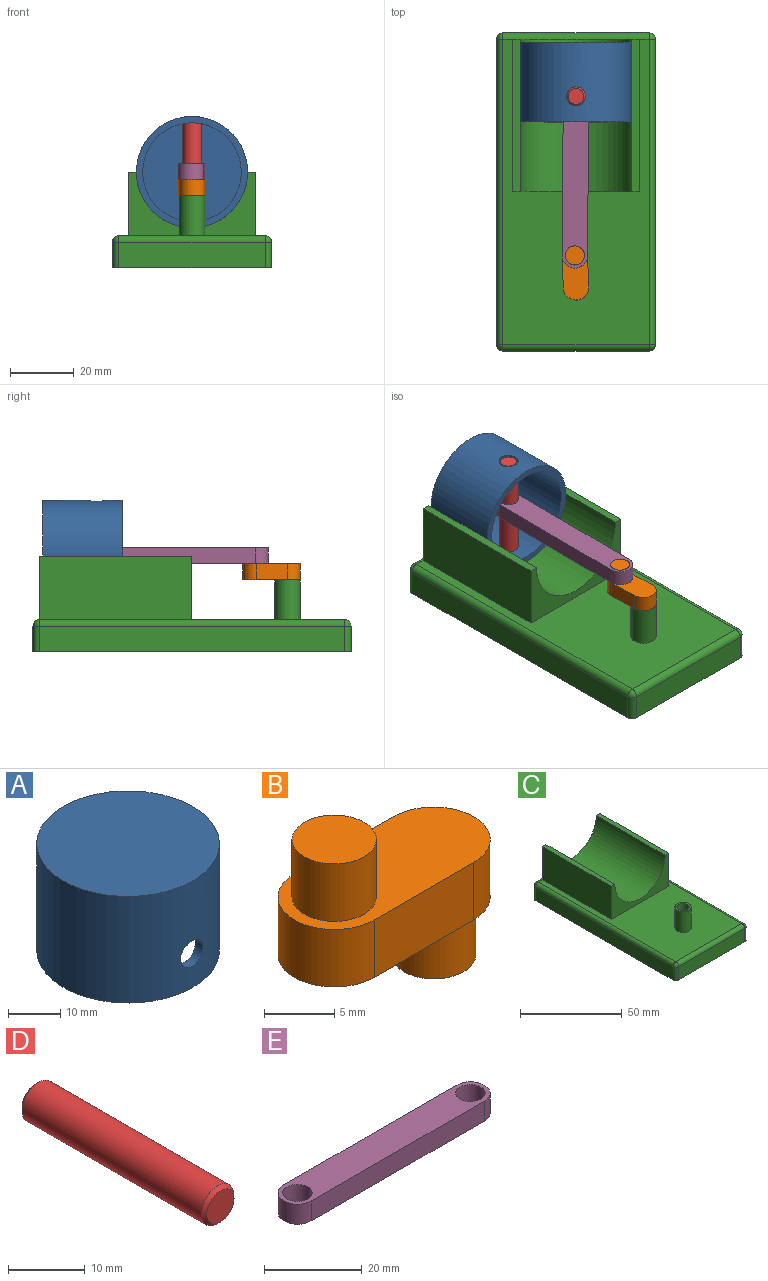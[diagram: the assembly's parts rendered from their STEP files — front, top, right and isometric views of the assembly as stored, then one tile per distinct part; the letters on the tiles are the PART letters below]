
ASSEMBLY  parts=5 mates=5
PART A: 7 faces, bbox 35x35x25 mm
  f0: cylinder r=17.5mm len=35mm, axis (0,0,-1), area 2691.8mm2, adj f1,f2,f5,f6
  f1: plane 35x35mm, normal (0,0,1), area 962.1mm2, adj f0
  f2: plane 35x35mm, normal (0,0,-1), area 207.3mm2, adj f0,f3
  f3: cylinder r=15.5mm len=31mm, axis (0,0,-1), area 2182.9mm2, adj f2,f4,f5,f6
  f4: plane 31x31mm, normal (0,0,-1), area 754.8mm2, adj f3
  f5: cylinder r=3mm len=6mm, axis (0,-1,0), area 38mm2, adj f0,f3
  f6: cylinder r=3mm len=6mm, axis (0,-1,0), area 38mm2, adj f0,f3
PART B: 10 faces, bbox 18x8x15 mm
  f0: cylinder r=4mm len=8mm, axis (0,0,-1), area 62.8mm2, adj f1,f3,f4,f5
  f1: plane 10x5mm, normal (0,1,0), area 50mm2, adj f0,f2,f4,f5
  f2: cylinder r=4mm len=8mm, axis (0,0,-1), area 62.8mm2, adj f1,f3,f4,f5
  f3: plane 10x5mm, normal (0,-1,0), area 50mm2, adj f0,f2,f4,f5
  f4: plane 18x8mm, normal (0,0,1), area 102mm2, adj f0,f1,f2,f3,f6
  f5: plane 18x8mm, normal (0,0,-1), area 102mm2, adj f0,f1,f2,f3,f8
  f6: cylinder r=3mm len=6mm, axis (0,0,-1), area 94.2mm2, adj f4,f7
  f7: plane 6x6mm, normal (0,0,1), area 28.3mm2, adj f6
  f8: cylinder r=3mm len=6mm, axis (0,0,1), area 94.2mm2, adj f5,f9
  f9: plane 6x6mm, normal (0,0,-1), area 28.3mm2, adj f8
PART C: 29 faces, bbox 50x100x30 mm
  f0: plane 48x2.5mm, normal (0,0,1), area 120mm2, adj f1,f22,f23,f24
  f1: plane 40x20mm, normal (0,1,0), area 318.9mm2, adj f0,f11,f20,f21,f22,f24
  f2: plane 96x46mm, normal (0,0,1), area 2445.7mm2, adj f11,f12,f16,f17,f20,f22,f23,f25
  f3: plane 96x8mm, normal (-1,0,0), area 768mm2, adj f7,f10,f16,f19
  f4: plane 46x8mm, normal (0,-1,0), area 368mm2, adj f7,f13,f17,f19
  f5: plane 96x8mm, normal (1,0,0), area 768mm2, adj f7,f8,f12,f13
  f6: plane 46x8mm, normal (0,1,0), area 368mm2, adj f7,f8,f10,f11
  f7: plane 100x50mm, normal (0,0,-1), area 4996.6mm2, adj f3,f4,f5,f6,f8,f10,f13,f19
  f8: cylinder r=2mm len=8mm, axis (0,0,-1), area 25.1mm2, adj f5,f6,f7,f9
  f9: sphere r=2mm, area 6.3mm2, adj f8,f11,f12
  f10: cylinder r=2mm len=8mm, axis (0,0,1), area 25.1mm2, adj f3,f6,f7,f14
  f11: cylinder r=2mm len=46mm, axis (1,0,0), area 144.5mm2, adj f1,f2,f6,f9,f14
  f12: cylinder r=2mm len=96mm, axis (0,-1,0), area 301.6mm2, adj f2,f5,f9,f15
  f13: cylinder r=2mm len=8mm, axis (0,0,-1), area 25.1mm2, adj f4,f5,f7,f15
  f14: sphere r=2mm, area 6.3mm2, adj f10,f11,f16
  f15: sphere r=2mm, area 6.3mm2, adj f12,f13,f17
  f16: cylinder r=2mm len=96mm, axis (0,1,0), area 301.6mm2, adj f2,f3,f14,f18
  f17: cylinder r=2mm len=46mm, axis (-1,0,0), area 144.5mm2, adj f2,f4,f15,f18
  f18: sphere r=2mm, area 6.3mm2, adj f16,f17,f19
  f19: cylinder r=2mm len=8mm, axis (0,0,1), area 25.1mm2, adj f3,f4,f7,f18
  f20: plane 48x20mm, normal (1,0,0), area 960mm2, adj f1,f2,f21,f23
  f21: plane 48x2.5mm, normal (0,0,1), area 120mm2, adj f1,f20,f23,f24
  f22: plane 48x20mm, normal (-1,0,0), area 960mm2, adj f0,f1,f2,f23
  f23: plane 40x20mm, normal (0,-1,0), area 318.9mm2, adj f0,f2,f20,f21,f22,f24
  f24: cylinder r=17.5mm len=48mm, axis (0,-1,0), area 2638.9mm2, adj f0,f1,f21,f23
  f25: cylinder r=4mm len=12.5mm, axis (0,0,-1), area 314.2mm2, adj f2,f26
  f26: plane 8x8mm, normal (0,0,1), area 22mm2, adj f25,f27
  f27: cylinder r=3mm len=15mm, axis (0,0,1), area 282.7mm2, adj f26,f28
  f28: plane 6x6mm, normal (0,0,1), area 28.3mm2, adj f27
PART D: 5 faces, bbox 6x34x6 mm
  f0: cylinder r=3mm len=33mm, axis (0,-1,0), area 622mm2, adj f3,f4
  f1: plane 5x5mm, normal (0,1,0), area 19.6mm2, adj f3
  f2: plane 5x5mm, normal (0,-1,0), area 19.6mm2, adj f4
  f3: cone r=3mm half-angle=45deg, axis (0,-1,0), area 12.2mm2, adj f0,f1
  f4: cone r=2.5mm half-angle=45deg, axis (0,1,0), area 12.2mm2, adj f0,f2
PART E: 8 faces, bbox 58x8x5 mm
  f0: cylinder r=4mm len=8mm, axis (0,0,-1), area 62.8mm2, adj f1,f3,f4,f5
  f1: plane 50x5mm, normal (0,1,0), area 250mm2, adj f0,f2,f4,f5
  f2: cylinder r=4mm len=8mm, axis (0,0,-1), area 62.8mm2, adj f1,f3,f4,f5
  f3: plane 50x5mm, normal (0,-1,0), area 250mm2, adj f0,f2,f4,f5
  f4: plane 58x8mm, normal (0,0,1), area 393.7mm2, adj f0,f1,f2,f3,f6,f7
  f5: plane 58x8mm, normal (0,0,-1), area 393.7mm2, adj f0,f1,f2,f3,f6,f7
  f6: cylinder r=3mm len=6mm, axis (0,0,1), area 94.2mm2, adj f4,f5
  f7: cylinder r=3mm len=6mm, axis (0,0,1), area 94.2mm2, adj f4,f5
PLACE A rot(axis=(-1,0,0),90deg) t=(0,71.99,30)mm
PLACE B rot(axis=(0,0,-1),87.9deg) t=(-0.37,29.99,22.65)mm
PLACE C at identity fixed
PLACE D rot(axis=(-1,0,0),90deg) t=(0,79.99,47.15)mm
PLACE E rot(axis=(0,0,-1),90.4deg) t=(0,79.99,27.65)mm
MATE revolute E.f2 <-> D.f0  axis (0,0,1) through (0,79.99,30.15)mm
MATE cylindrical B.f0 <-> C.f25  axis (0,0,1) through (0,20,20.15)mm
MATE slider A.f0 <-> C.f24  axis (0,-1,0) through (0,84.49,30)mm
MATE revolute D.f0 <-> A.f5  axis (0,0,1) through (0,79.99,30.15)mm
MATE revolute B.f2 <-> E.f0  axis (0,0,1) through (-0.37,29.99,27.65)mm
